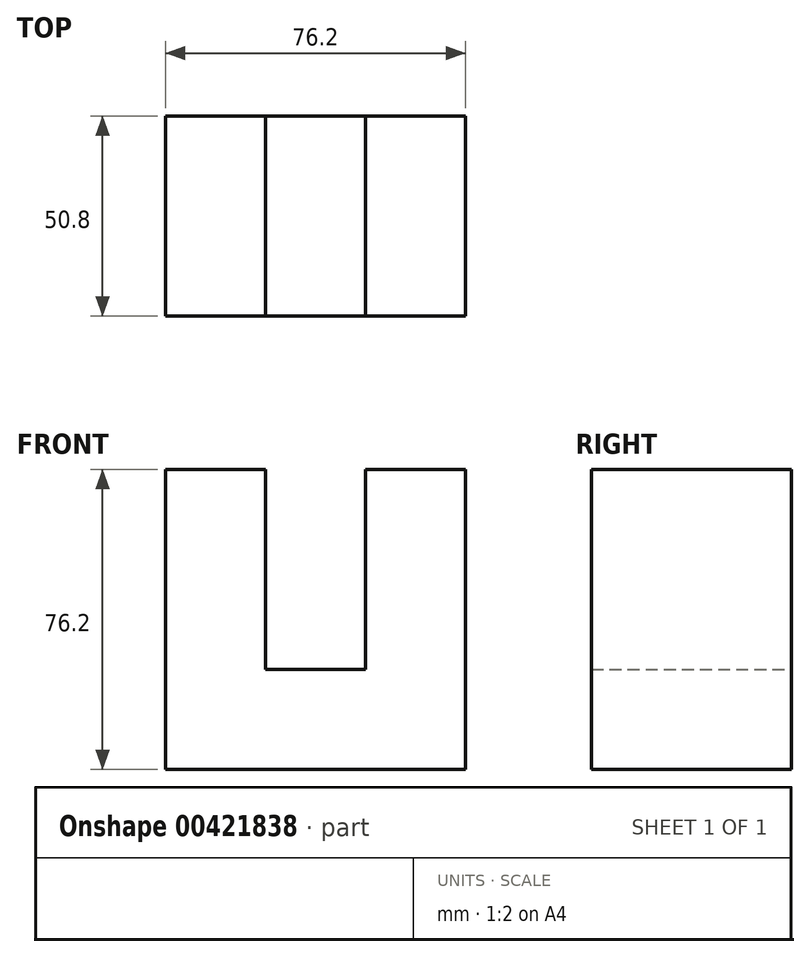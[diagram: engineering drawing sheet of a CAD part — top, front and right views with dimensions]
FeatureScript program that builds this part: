
annotation { "Feature Type Name" : "Feature", "Feature Type Description" : "" }
export const myFeature = defineFeature(function(context is Context, id is Id, definition is map)
    precondition{}
    {
        {
            var Q0;
            Q0=qCreatedBy(makeId("Front.planeOp"),FACE);
            var sketch = newSketch(context, id + "F0", { "sketchPlane" : qUnion([Q0])});
            skLineSegment(sketch, "E0", {"start": v(0, 0) * mm, "end": v(76.2, 0) * mm});
            skLineSegment(sketch, "E1", {"start": v(0, 0) * mm, "end": v(0, 76.2) * mm});
            skLineSegment(sketch, "E2", {"start": v(0, 76.2) * mm, "end": v(25.4, 76.2) * mm});
            skLineSegment(sketch, "E3", {"start": v(25.4, 76.2) * mm, "end": v(25.4, 25.4) * mm});
            skLineSegment(sketch, "E4", {"start": v(76.2, 0) * mm, "end": v(76.2, 76.2) * mm});
            skLineSegment(sketch, "E5", {"start": v(76.2, 76.2) * mm, "end": v(50.8, 76.2) * mm});
            skLineSegment(sketch, "E6", {"start": v(50.8, 76.2) * mm, "end": v(50.8, 25.4) * mm});
            skLineSegment(sketch, "E7", {"start": v(50.8, 25.4) * mm, "end": v(25.4, 25.4) * mm});
            skSolve(sketch);
        }
        {
            var Q0;
            Q0=makeQuery(id+"F0.imprint","IMPRINT",FACE,{"disambiguationData":[TD([[makeQuery(id+"F0.imprint","IMPRINT",EDGE,{"derivedFrom":sQuery(id+"F0.wireOp",EDGE,"E0")}),1.0]])]});
            extrude(context, id + "F1", {"entities" : qUnion([Q0]), "depth" : 50.8 * mm});
        }
    });
